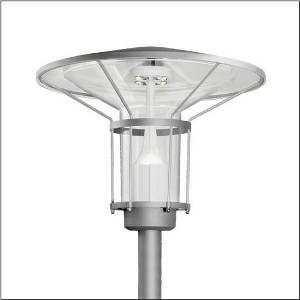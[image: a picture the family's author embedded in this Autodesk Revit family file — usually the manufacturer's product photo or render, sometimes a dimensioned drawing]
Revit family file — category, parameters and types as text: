
# Revit family: laterne_classic_iq___p1_0a_5xa5245lf14h_4a87
name_source: partatom
category: Lighting Fixtures
units: mm (PartAtom-declared; Revit-internal decimal feet)

## family parameters
Cut with Voids When Loaded = No
Host = Face
Light Source = No
Part Type = Normal
Room Calculation Point = No
Round Connector Dimension = Use Diameter
Shared = No

## types (1)
- --- (1 x LED, 1360 lm, 10 W, 4000K)
    Apparent Load = 10 VA
    CIE Flux Codes = 30 61 91 96 100
    Color Rendering = 70
    Color Temperature = 4000K
    Default Elevation = 1800 mm
    Description = Lantern Classic iQ, mast luminaire, Module 540 iQ-SR, primary light control with 3 zone facetted reflector, of plastic, silver coated, highly specular, structured, primary optical cover: cover, of PMMA, transparent, light distribution: P1.0a, light emission: direct distribution, primary light characteristic: strongly asymmetric, installation type: post-top, LED, High Power LED, rated luminous flux: 1.360lm, luminous efficacy: 136lm/W, light colour: 740, colour temperature: 4000K, control gear: iQ Street-Remote, control: pre-setting: logarithmic dimming characteristic, Street-Remote, Auto-Match, Temp-Guard, Lumen-Switch, Night-Set, Smart-Wire, Light-Fading, Desk-Remote (wireless, voltage-free reading and setting of iQ features in the workshop via application-optimized NFC function/RFID function), optimised constant luminous flux control (CLO 2.0), with terminal, 6-pole, max. 2.5mm², mains connection: 230..240V, AC, 50/60Hz, start of lifetime: 10W, end of service life: 10W, reduction: 5W, luminaire housing, upper part, of glass-fibre reinforced polyester, coated, Siteco® metallic grey (DB 702S), diameter: 750mm, height: 596mm, spigot size: d x l = 76 x 70mm (post-top) | with reducer (optional accessory) 60 x 70mm, mounting height: 3..5m, post-top mast mounting element, of diecast aluminium, coated, Siteco® metallic grey (DB 702S), Module 540 iQ-SR, traffic white (RAL 9016), equipment: standard, protection rating (complete): IP65, insulation class (complete): insulation class II (safety insulation), certification: CE, ENEC, VDE, packaging unit: 1 piece

Light Distribution: P1.0a
    Height = 596 mm
    Lamp = 1 x LED
    Lamp Light Flux = 1360 lm
    Lamp Power = 10 W
    Lamp count = 1
    Length = 750 mm
    Luminous efficacy = 136 lm/W
    Manufacturer = Siteco
    ModVariant = No
    Model = 5XA5245LF14H
    Number of Poles = 1
    OnlyDefault = Yes
    Power Factor = 1
    Product Name = Laterne Classic iQ | P1.0a
    Product group = mast luminaire | pylon top
    ProductGroupID = 6100
    Protection Class = Protection class II
    Protection Degree = IP 65
    RLX_Detail_Level = 1
    RLX_Emergency_Light_Flux = 0 lm
    RLX_Emergency_Type = 0
    RLX_Emergency_Type_DB = No
    RlxData = <blob elided: 97925 chars, md5=870f56ab>
    Socket = socket
    Standby Power = 0 W
    System Light Flux = 1360 lm
    System Power = 10 W
    Type Comments = factory setting: luminous flux: 100 % | dim-lin: 254 | 401 mA
    Type Image = l_1006052.jpg
    URL = http://relux.com
    VarID = @adj_181679
    Voltage = 0 V
    Weight = 0.00 kg
    Width = 0 mm  [stored 0 ft]

note: [stored X ft] marks values corroborated as IEEE doubles in the binary element streams (Revit-internal decimal feet)

## geometry (parser evidence)
native form markers: Blend x4, Sweep x8
no freeform markers — native parametric forms only
